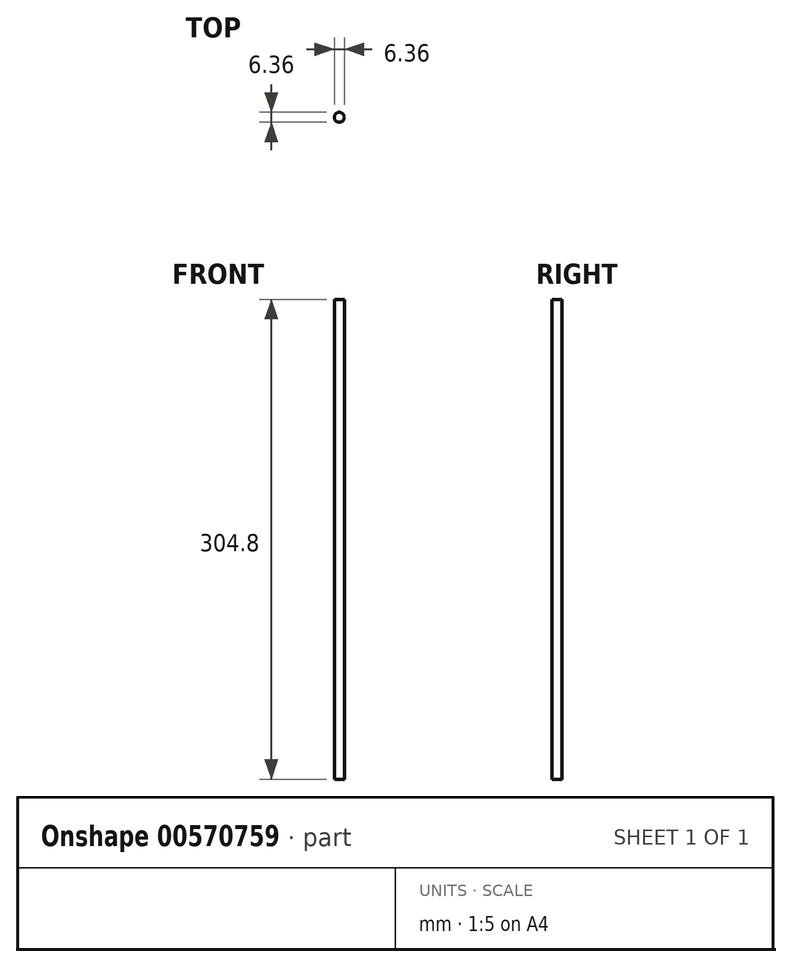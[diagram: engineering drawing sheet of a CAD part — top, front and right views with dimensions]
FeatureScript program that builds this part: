
annotation { "Feature Type Name" : "Feature", "Feature Type Description" : "" }
export const myFeature = defineFeature(function(context is Context, id is Id, definition is map)
    precondition{}
    {
        {
            var Q0;
            Q0=qCreatedBy(makeId("Top.planeOp"),FACE);
            var sketch = newSketch(context, id + "F0", { "sketchPlane" : qUnion([Q0])});
            skCircle(sketch, "E0", {"center": v(0, 0) * mm, "radius": 3.18 * mm});
            skSolve(sketch);
        }
        {
            var Q0;
            Q0=makeQuery(id+"F0.imprint","IMPRINT",FACE,{"disambiguationData":[TD([[makeQuery(id+"F0.imprint","IMPRINT",EDGE,{"derivedFrom":sQuery(id+"F0.wireOp",EDGE,"E0")}),1.0]])]});
            extrude(context, id + "F1", {"entities" : qUnion([Q0]), "depth" : 304.8 * mm, "offsetDistance" : 25.4 * mm});
        }
    });
